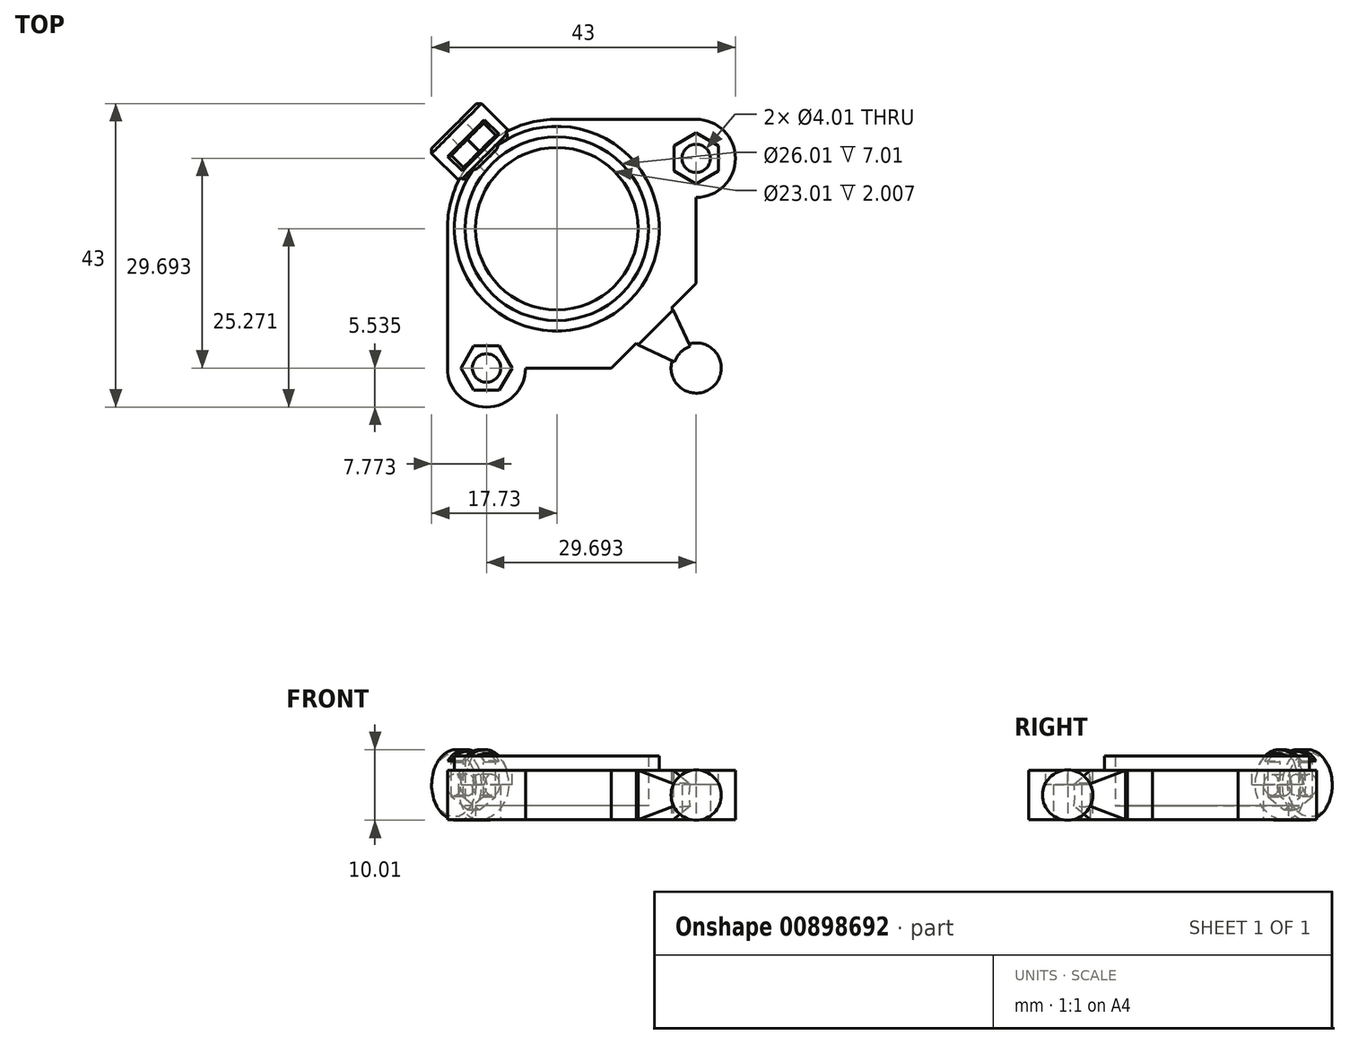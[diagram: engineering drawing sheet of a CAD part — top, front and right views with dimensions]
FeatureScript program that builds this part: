
annotation { "Feature Type Name" : "Feature", "Feature Type Description" : "" }
export const myFeature = defineFeature(function(context is Context, id is Id, definition is map)
    precondition{}
    {
        {
            var Q0;
            Q0=qCreatedBy(makeId("Top.planeOp"),FACE);
            var sketch = newSketch(context, id + "F0", { "sketchPlane" : qUnion([Q0])});
            skArc(sketch, "E0", {"start": v(3.05, -1.27) * mm, "mid": v(0, 3.3) * mm, "end": v(-3.05, -1.27) * mm, "construction": true});
            skArc(sketch, "E1", {"start": v(-32.87, 34.65) * mm, "mid": v(-35.92, 39.22) * mm, "end": v(-38.97, 34.65) * mm, "construction": true});
            skArc(sketch, "E2", {"start": v(38.97, 34.65) * mm, "mid": v(35.92, 39.22) * mm, "end": v(32.87, 34.65) * mm, "construction": true});
            skCircle(sketch, "E3", {"center": v(0, 35.92) * mm, "radius": 14.29 * mm, "construction": true});
            skArc(sketch, "E4.0", {"start": v(-35.92, 46.84) * mm, "mid": v(-46.06, 39.97) * mm, "end": v(-43.45, 28) * mm, "construction": true});
            skArc(sketch, "E5.0", {"start": v(0, 56.56) * mm, "mid": v(-12.05, 52.67) * mm, "end": v(-19.57, 42.48) * mm, "construction": true});
            skArc(sketch, "E6.0", {"start": v(43.45, 28) * mm, "mid": v(46.06, 39.97) * mm, "end": v(35.92, 46.84) * mm, "construction": true});
            skArc(sketch, "E7.0", {"start": v(-6.65, -7) * mm, "mid": v(-5.57, -7.88) * mm, "end": v(-4.38, -8.6) * mm, "construction": true});
            skLineSegment(sketch, "E8", {"start": v(-35.92, 46.84) * mm, "end": v(-28.3, 46.84) * mm, "construction": true});
            skLineSegment(sketch, "E9", {"start": v(30.37, 46.84) * mm, "end": v(35.92, 46.84) * mm, "construction": true});
            skLineSegment(sketch, "E10", {"start": v(43.45, 28) * mm, "end": v(40.52, 25.22) * mm, "construction": true});
            skLineSegment(sketch, "E11", {"start": v(-6.65, -7) * mm, "end": v(-32.87, 17.95) * mm, "construction": true});
            skCircle(sketch, "E12", {"center": v(-35.92, 35.92) * mm, "radius": 3.05 * mm, "construction": true});
            skCircle(sketch, "E13", {"center": v(35.92, 35.92) * mm, "radius": 3.05 * mm, "construction": true});
            skCircle(sketch, "E14", {"center": v(0, 0) * mm, "radius": 3.05 * mm, "construction": true});
            skLineSegment(sketch, "E15", {"start": v(-32.87, 35.92) * mm, "end": v(-32.87, 17.95) * mm, "construction": true});
            skLineSegment(sketch, "E16", {"start": v(-38.97, 35.92) * mm, "end": v(-38.97, 25.88) * mm, "construction": true});
            skLineSegment(sketch, "E17", {"start": v(-3.05, 0) * mm, "end": v(-3.05, -7.79) * mm, "construction": true});
            skLineSegment(sketch, "E18", {"start": v(3.05, 0) * mm, "end": v(3.05, -7.79) * mm, "construction": true});
            skPoint(sketch, "E19", {"position": v(-3.05, -1.27) * mm});
            skPoint(sketch, "E20", {"position": v(3.05, -1.27) * mm});
            skArc(sketch, "E21.trimOffspring", {"start": v(4.38, -8.6) * mm, "mid": v(5.57, -7.88) * mm, "end": v(6.65, -7) * mm, "construction": true});
            skLineSegment(sketch, "E22.trimOffspring", {"start": v(-40.52, 25.22) * mm, "end": v(-43.45, 28) * mm, "construction": true});
            skPoint(sketch, "E23.visualSharp", {"position": v(-38.97, 23.75) * mm});
            skArc(sketch, "E23.filletArc", {"start": v(-40.52, 25.22) * mm, "mid": v(-39.52, 25.04) * mm, "end": v(-38.97, 25.88) * mm, "construction": true});
            skPoint(sketch, "E24.visualSharp", {"position": v(-3.05, -9.16) * mm});
            skArc(sketch, "E24.filletArc", {"start": v(-4.38, -8.6) * mm, "mid": v(-3.49, -8.57) * mm, "end": v(-3.05, -7.79) * mm, "construction": true});
            skPoint(sketch, "E25.visualSharp", {"position": v(3.05, -9.16) * mm});
            skArc(sketch, "E25.filletArc", {"start": v(3.05, -7.79) * mm, "mid": v(3.49, -8.57) * mm, "end": v(4.38, -8.6) * mm, "construction": true});
            skLineSegment(sketch, "E26", {"start": v(32.87, 35.92) * mm, "end": v(32.87, 17.95) * mm, "construction": true});
            skLineSegment(sketch, "E27", {"start": v(38.97, 35.92) * mm, "end": v(38.97, 25.88) * mm, "construction": true});
            skLineSegment(sketch, "E28.trimOffspring", {"start": v(32.87, 17.95) * mm, "end": v(6.65, -7) * mm, "construction": true});
            skPoint(sketch, "E29.visualSharp", {"position": v(38.97, 23.75) * mm});
            skArc(sketch, "E30.filletArc", {"start": v(38.97, 25.88) * mm, "mid": v(39.52, 25.04) * mm, "end": v(40.52, 25.22) * mm, "construction": true});
            skLineSegment(sketch, "E31", {"start": v(-35.92, 35.92) * mm, "end": v(35.92, 35.92) * mm, "construction": true});
            skArc(sketch, "E32.trimOffspring", {"start": v(-19.57, 42.48) * mm, "mid": v(-23.42, 45.7) * mm, "end": v(-28.3, 46.84) * mm, "construction": true});
            skCircle(sketch, "E33", {"center": v(-9.96, 16.19) * mm, "radius": 2 * mm});
            skCircle(sketch, "E34", {"center": v(19.74, 45.88) * mm, "radius": 2 * mm});
            skPoint(sketch, "E35.start.orphan", {"position": v(0, 56.56) * mm});
            skLineSegment(sketch, "E36", {"start": v(0, 56.56) * mm, "end": v(19.74, 56.56) * mm, "construction": true});
            skArc(sketch, "E37.trimOffspring", {"start": v(30.37, 46.84) * mm, "mid": v(26.94, 53.76) * mm, "end": v(19.74, 56.56) * mm, "construction": true});
            skArc(sketch, "E38", {"start": v(0, 51.41) * mm, "mid": v(-10.96, 46.88) * mm, "end": v(-15.5, 35.92) * mm});
            skCircle(sketch, "E39", {"center": v(0, 35.92) * mm, "radius": 11.5 * mm});
            skArc(sketch, "E40", {"start": v(-15.5, 16.19) * mm, "mid": v(-9.96, 10.65) * mm, "end": v(-4.42, 16.19) * mm});
            skArc(sketch, "E41", {"start": v(19.74, 40.34) * mm, "mid": v(25.27, 45.88) * mm, "end": v(19.74, 51.41) * mm});
            skLineSegment(sketch, "E42", {"start": v(-15.5, 35.92) * mm, "end": v(-15.5, 16.19) * mm});
            skLineSegment(sketch, "E43", {"start": v(0, 51.41) * mm, "end": v(19.74, 51.41) * mm});
            skLineSegment(sketch, "E44", {"start": v(-4.42, 16.19) * mm, "end": v(7.74, 16.19) * mm});
            skLineSegment(sketch, "E45", {"start": v(19.74, 28.18) * mm, "end": v(19.74, 40.34) * mm});
            skLineSegment(sketch, "E46", {"start": v(19.74, 28.18) * mm, "end": v(7.74, 16.19) * mm});
            skCircle(sketch, "E47", {"center": v(0, 35.92) * mm, "radius": 13 * mm});
            skPoint(sketch, "E48.orphan", {"position": v(19.74, 16.19) * mm});
            skLineSegment(sketch, "E49", {"start": v(0, 35.92) * mm, "end": v(19.74, 16.19) * mm, "construction": true});
            skLineSegment(sketch, "E50", {"start": v(11.26, 19.7) * mm, "end": v(17.26, 13.7) * mm});
            skLineSegment(sketch, "E51", {"start": v(17.26, 13.7) * mm, "end": v(22.21, 18.66) * mm});
            skLineSegment(sketch, "E52", {"start": v(22.21, 18.66) * mm, "end": v(16.22, 24.66) * mm});
            skSolve(sketch);
        }
        {
            var Q0;
            Q0=makeQuery(id+"F0.imprint","IMPRINT",FACE,{"disambiguationData":[TD([[makeQuery(id+"F0.imprint","IMPRINT",EDGE,{"derivedFrom":sQuery(id+"F0.wireOp",EDGE,"E33")}),-1.0]])]});
            var Q1;
            {var subQ0=sQuery(id+"F0.wireOp",EDGE,"E50");Q1=makeQuery(id+"F0.imprint","IMPRINT",FACE,{"disambiguationData":[TD([[makeQuery(id+"F0.imprint","IMPRINT",EDGE,{"derivedFrom":subQ0}),1.0]])]});}
            extrude(context, id + "F1", {"entities" : qUnion([Q0, Q1]), "depth" : 7 * mm, "offsetDistance" : 25.4 * mm});
        }
        {
            var Q0;
            Q0=makeQuery(id+"F1.opExtrude","CAP_EDGE",EDGE,{"disambiguationData":[OSD([sQuery(id+"F0.wireOp",EDGE,"E51")])],"isStart":false});
            var Q1;
            Q1=makeQuery(id+"F1.opExtrude","SWEPT_EDGE",EDGE,{"disambiguationData":[OSD([sQuery(id+"F0.wireOp",EDGE,"E51"),sQuery(id+"F0.wireOp",EDGE,"E52")])]});
            var Q2;
            Q2=makeQuery(id+"F1.opExtrude","SWEPT_EDGE",EDGE,{"disambiguationData":[OSD([sQuery(id+"F0.wireOp",EDGE,"E50"),sQuery(id+"F0.wireOp",EDGE,"E51")])]});
            var Q3;
            Q3=makeQuery(id+"F1.opExtrude","CAP_EDGE",EDGE,{"disambiguationData":[OSD([sQuery(id+"F0.wireOp",EDGE,"E51")])],"isStart":true});
            chamfer(context, id + "F2", {"entities" : qUnion([Q0, Q1, Q2, Q3]), "chamferType" : ChamferType.OFFSET_ANGLE, "width" : 8.13 * mm, "oppositeDirection" : false, "angle" : 20 * degree, "tangentPropagation" : true});
        }
        {
            var Q0;
            Q0=makeQuery(id+"F0.imprint","IMPRINT",FACE,{"disambiguationData":[TD([[makeQuery(id+"F0.imprint","IMPRINT",EDGE,{"derivedFrom":sQuery(id+"F0.wireOp",EDGE,"E39")}),-1.0]])]});
            extrude(context, id + "F3", {"entities" : qUnion([Q0]), "operationType" : NewBodyOperationType.ADD, "depth" : 2 * mm, "offsetDistance" : 25.4 * mm});
        }
        {
            var Q0;
            Q0=makeQuery(id+"F1.opExtrude","CAP_FACE",FACE,{"disambiguationData":[OSD([sQuery(id+"F0.wireOp",EDGE,"E33"),sQuery(id+"F0.wireOp",EDGE,"E34"),sQuery(id+"F0.wireOp",EDGE,"E38"),sQuery(id+"F0.wireOp",EDGE,"E40"),sQuery(id+"F0.wireOp",EDGE,"E41"),sQuery(id+"F0.wireOp",EDGE,"E42"),sQuery(id+"F0.wireOp",EDGE,"E43"),sQuery(id+"F0.wireOp",EDGE,"E44"),sQuery(id+"F0.wireOp",EDGE,"E45"),sQuery(id+"F0.wireOp",EDGE,"E46"),sQuery(id+"F0.wireOp",EDGE,"E47"),sQuery(id+"F0.wireOp",EDGE,"E50"),sQuery(id+"F0.wireOp",EDGE,"E51"),sQuery(id+"F0.wireOp",EDGE,"E52")])],"isStart":false});
            var sketch = newSketch(context, id + "F4", { "sketchPlane" : qUnion([Q0])});
            skCircle(sketch, "E53", {"center": v(0, 35.92) * mm, "radius": 14.5 * mm});
            skCircle(sketch, "E54.cCircle", {"center": v(19.74, 45.88) * mm, "radius": 3.6 * mm, "construction": true});
            skLineSegment(sketch, "E54.0", {"start": v(19.74, 42.27) * mm, "end": v(16.61, 44.07) * mm});
            skLineSegment(sketch, "E54.1", {"start": v(16.61, 44.07) * mm, "end": v(16.61, 47.68) * mm});
            skLineSegment(sketch, "E54.2", {"start": v(16.61, 47.68) * mm, "end": v(19.74, 49.48) * mm});
            skLineSegment(sketch, "E54.3", {"start": v(19.74, 49.48) * mm, "end": v(22.86, 47.68) * mm});
            skLineSegment(sketch, "E54.4", {"start": v(22.86, 47.68) * mm, "end": v(22.86, 44.07) * mm});
            skLineSegment(sketch, "E54.5", {"start": v(22.86, 44.07) * mm, "end": v(19.74, 42.27) * mm});
            skCircle(sketch, "E55.cCircle", {"center": v(-9.96, 16.19) * mm, "radius": 3.6 * mm, "construction": true});
            skLineSegment(sketch, "E55.0", {"start": v(-6.35, 16.19) * mm, "end": v(-8.15, 13.06) * mm});
            skLineSegment(sketch, "E55.1", {"start": v(-8.15, 13.06) * mm, "end": v(-11.76, 13.06) * mm});
            skLineSegment(sketch, "E55.2", {"start": v(-11.76, 13.06) * mm, "end": v(-13.56, 16.19) * mm});
            skLineSegment(sketch, "E55.3", {"start": v(-13.56, 16.19) * mm, "end": v(-11.76, 19.3) * mm});
            skLineSegment(sketch, "E55.4", {"start": v(-11.76, 19.3) * mm, "end": v(-8.15, 19.3) * mm});
            skLineSegment(sketch, "E55.5", {"start": v(-8.15, 19.3) * mm, "end": v(-6.35, 16.19) * mm});
            skSolve(sketch);
        }
        {
            var Q0;
            Q0=makeQuery(id+"F4.imprint","IMPRINT",FACE,{"disambiguationData":[TD([[makeQuery(id+"F4.imprint","IMPRINT",EDGE,{"derivedFrom":sQuery(id+"F4.wireOp",EDGE,"E53")}),1.0]])]});
            extrude(context, id + "F5", {"entities" : qUnion([Q0]), "operationType" : NewBodyOperationType.ADD, "depth" : 2 * mm, "offsetDistance" : 25.4 * mm});
        }
        {
            var Q0;
            Q0=makeQuery(id+"F4.imprint","IMPRINT",FACE,{"disambiguationData":[TD([[makeQuery(id+"F4.imprint","IMPRINT",EDGE,{"derivedFrom":sQuery(id+"F4.wireOp",EDGE,"E54.0")}),-1.0]])]});
            var Q1;
            Q1=makeQuery(id+"F4.imprint","IMPRINT",FACE,{"disambiguationData":[TD([[makeQuery(id+"F4.imprint","IMPRINT",EDGE,{"derivedFrom":sQuery(id+"F4.wireOp",EDGE,"E55.0")}),-1.0]])]});
            extrude(context, id + "F6", {"entities" : qUnion([Q0, Q1]), "operationType" : NewBodyOperationType.REMOVE, "oppositeDirection" : true, "depth" : 2 * mm, "offsetDistance" : 25.4 * mm});
        }
        {
            var Q0;
            Q0=makeQuery(id+"F1.opExtrude","SWEPT_FACE",FACE,{"disambiguationData":[OSD([sQuery(id+"F0.wireOp",EDGE,"E51")])]});
            var sketch = newSketch(context, id + "F7", { "sketchPlane" : qUnion([Q0])});
            skArc(sketch, "E56", {"start": v(25.4, 7.06) * mm, "mid": v(21.84, 3.5) * mm, "end": v(25.4, -0.05) * mm});
            skPoint(sketch, "E56.centerSnap0", {"position": v(25.95, 3.5) * mm});
            skPoint(sketch, "E56.centerSnap1", {"position": v(25.4, 4.05) * mm});
            skLineSegment(sketch, "E57", {"start": v(25.4, 7.06) * mm, "end": v(25.4, -0.05) * mm});
            skPoint(sketch, "E57.startSnap0", {"position": v(25.4, 2.96) * mm});
            skSolve(sketch);
        }
        {
            var Q0;
            {var subQ4=sQuery(id+"F7.wireOp",EDGE,"E56");Q0=makeQuery(id+"F7.imprint","IMPRINT",FACE,{"disambiguationData":[TD([[makeQuery(id+"F7.imprint","IMPRINT",EDGE,{"derivedFrom":subQ4}),1.0]])]});}
            var Q1;
            {var subQ1=sQuery(id+"F0.wireOp",EDGE,"E51");var subQ2=makeQuery(id+"F1.opExtrude","SWEPT_FACE",FACE,{"disambiguationData":[OSD([subQ1])]});var subQ7=makeQuery(id+"F2.opChamfer","BLEND_EDGE",EDGE,{"blendedFrom":[makeQuery(id+"F1.opExtrude","SWEPT_EDGE",EDGE,{"disambiguationData":[OSD([sQuery(id+"F0.wireOp",EDGE,"E50"),subQ1])]}),subQ2],"blendedInto":[subQ2]});Q1=makeQuery(id+"F7.imprint","IMPRINT",FACE,{"disambiguationData":[TD([[makeQuery(id+"F7.imprint","IMPRINT",EDGE,{"derivedFrom":subQ7}),1.0]])]});}
            var Q2;
            Q2=sQuery(id+"F7.wireOp",EDGE,"E57");
            revolve(context, id + "F8", {"operationType" : NewBodyOperationType.ADD, "surfaceOperationType" : NewSurfaceOperationType.NEW, "entities" : qUnion([Q0, Q1]), "axis" : qUnion([Q2]), "revolveType" : RevolveType.FULL});
        }
        {
            var Q0;
            {var subQ0=sQuery(id+"F0.wireOp",EDGE,"E46");Q0=makeQuery(id+"F1.opExtrude","SWEPT_FACE",FACE,{"disambiguationData":[OSD([subQ0]),TDD([makeQuery(id+"F0.imprint","IMPRINT",EDGE,{"disambiguationData":[TD([[makeQuery(id+"F0.imprint","INTERSECT",VERTEX,{"derivedFrom":[sQuery(id+"F0.wireOp",EDGE,"E45"),subQ0]}),-1.0]])],"derivedFrom":subQ0})])]});}
            cPlane(context, id + "F9", {"entities" : qUnion([Q0]), "cplaneType" : CPlaneType.OFFSET, "offset" : 40 * mm, "oppositeDirection" : true, "width" : 152.4 * mm, "height" : 152.4 * mm});
        }
        {
            var Q0;
            Q0=qCreatedBy(id+"F9.planeOp",FACE);
            var sketch = newSketch(context, id + "F10", { "sketchPlane" : qUnion([Q0])});
            skCircle(sketch, "E58", {"center": v(25.4, 3.5) * mm, "radius": 3.56 * mm, "construction": true});
            skCircle(sketch, "E59", {"center": v(25.4, 4.95) * mm, "radius": 1.5 * mm});
            skCircle(sketch, "E60", {"center": v(25.4, 4.95) * mm, "radius": 5 * mm});
            skLineSegment(sketch, "E61", {"start": v(31, 0) * mm, "end": v(18.63, -0.11) * mm, "construction": true});
            skLineSegment(sketch, "E62", {"start": v(25.4, 4.95) * mm, "end": v(25.4, 3.5) * mm, "construction": true});
            skSolve(sketch);
        }
        {
            var Q0;
            Q0=makeQuery(id+"F10.imprint","IMPRINT",FACE,{"disambiguationData":[TD([[makeQuery(id+"F10.imprint","IMPRINT",EDGE,{"derivedFrom":sQuery(id+"F10.wireOp",EDGE,"E59")}),-1.0]])]});
            extrude(context, id + "F11", {"entities" : qUnion([Q0]), "operationType" : NewBodyOperationType.ADD, "depth" : 6.6 * mm, "offsetDistance" : 25.4 * mm});
        }
        {
            var Q0;
            Q0=makeQuery(id+"F10.imprint","IMPRINT",FACE,{"disambiguationData":[TD([[makeQuery(id+"F10.imprint","IMPRINT",EDGE,{"derivedFrom":sQuery(id+"F10.wireOp",EDGE,"E59")}),1.0]])]});
            extrude(context, id + "F12", {"entities" : qUnion([Q0]), "operationType" : NewBodyOperationType.REMOVE, "depth" : 12.7 * mm, "offsetDistance" : 25.4 * mm});
        }
        {
            var Q0;
            {var subQ0=sQuery(id+"F10.wireOp",EDGE,"E60");Q0=makeQuery(id+"F11.boolean.opBoolean","SPLIT",EDGE,{"disambiguationData":[TD([makeQuery(id+"F5.opExtrude","CAP_FACE",FACE,{"disambiguationData":[OSD([sQuery(id+"F0.wireOp",EDGE,"E47"),sQuery(id+"F4.wireOp",EDGE,"E53")])],"isStart":false})])],"derivedFrom":makeQuery(id+"F11.opExtrude","CAP_EDGE",EDGE,{"disambiguationData":[OSD([subQ0])],"isStart":false})});}
            var Q1;
            Q1=makeQuery(id+"F11.opExtrude","CAP_EDGE",EDGE,{"disambiguationData":[OSD([sQuery(id+"F10.wireOp",EDGE,"E60")])],"isStart":true});
            chamfer(context, id + "F13", {"entities" : qUnion([Q0, Q1]), "width" : 0.5 * mm, "tangentPropagation" : true});
        }
        {
            var Q0;
            Q0=qCreatedBy(makeId("Top.planeOp"),FACE);
            cPlane(context, id + "F14", {"entities" : qUnion([Q0]), "cplaneType" : CPlaneType.OFFSET, "offset" : 10 * mm, "width" : 152.4 * mm, "height" : 152.4 * mm});
        }
        {
            var Q0;
            Q0=qCreatedBy(id+"F14.planeOp",FACE);
            var sketch = newSketch(context, id + "F15", { "sketchPlane" : qUnion([Q0])});
            skArc(sketch, "E63.0", {"start": v(0, 51.41) * mm, "mid": v(-10.96, 46.88) * mm, "end": v(-15.5, 35.92) * mm, "construction": true});
            skLineSegment(sketch, "E64", {"start": v(-13.25, 44.59) * mm, "end": v(-8.67, 49.17) * mm});
            skLineSegment(sketch, "E65", {"start": v(-13.25, 44.59) * mm, "end": v(-14.95, 46.3) * mm});
            skLineSegment(sketch, "E66", {"start": v(-14.95, 46.3) * mm, "end": v(-10.37, 50.87) * mm});
            skLineSegment(sketch, "E67", {"start": v(-10.37, 50.87) * mm, "end": v(-8.67, 49.17) * mm});
            skLineSegment(sketch, "E68", {"start": v(0, 35.92) * mm, "end": v(-10.96, 46.88) * mm, "construction": true});
            skLineSegment(sketch, "E69", {"start": v(-10.37, 50.87) * mm, "end": v(0, 51.41) * mm, "construction": true});
            skLineSegment(sketch, "E70", {"start": v(-14.95, 46.3) * mm, "end": v(-15.5, 35.92) * mm, "construction": true});
            skSolve(sketch);
        }
        {
            var Q0;
            Q0=makeQuery(id+"F15.imprint","IMPRINT",FACE,{"disambiguationData":[TD([[makeQuery(id+"F15.imprint","IMPRINT",EDGE,{"derivedFrom":sQuery(id+"F15.wireOp",EDGE,"E64")}),1.0]])]});
            extrude(context, id + "F16", {"entities" : qUnion([Q0]), "operationType" : NewBodyOperationType.REMOVE, "oppositeDirection" : true, "depth" : 8.6 * mm, "offsetDistance" : 25.4 * mm});
        }
        {
            var Q0;
            Q0=makeQuery(id+"F16.boolean.opBoolean","COPY",EDGE,{"derivedFrom":makeQuery(id+"F16.opExtrude","CAP_EDGE",EDGE,{"disambiguationData":[OSD([sQuery(id+"F15.wireOp",EDGE,"E67")])],"isStart":false})});
            var Q1;
            Q1=makeQuery(id+"F16.boolean.opBoolean","COPY",EDGE,{"derivedFrom":makeQuery(id+"F16.opExtrude","CAP_EDGE",EDGE,{"disambiguationData":[OSD([sQuery(id+"F15.wireOp",EDGE,"E65")])],"isStart":false})});
            chamfer(context, id + "F17", {"entities" : qUnion([Q0, Q1]), "chamferType" : ChamferType.OFFSET_ANGLE, "width" : 1.85 * mm, "oppositeDirection" : false, "angle" : 60 * degree, "tangentPropagation" : true});
        }
        {
            var Q0;
            Q0=makeQuery(id+"F16.boolean.opBoolean","INTERSECT",EDGE,{"derivedFrom":[makeQuery(id+"F11.opExtrude","SWEPT_FACE",FACE,{"disambiguationData":[OSD([sQuery(id+"F10.wireOp",EDGE,"E60")])]}),makeQuery(id+"F16.opExtrude","SWEPT_FACE",FACE,{"disambiguationData":[OSD([sQuery(id+"F15.wireOp",EDGE,"E66")])]})]});
            var Q1;
            Q1=makeQuery(id+"F16.boolean.opBoolean","INTERSECT",EDGE,{"derivedFrom":[makeQuery(id+"F11.opExtrude","SWEPT_FACE",FACE,{"disambiguationData":[OSD([sQuery(id+"F10.wireOp",EDGE,"E60")])]}),makeQuery(id+"F16.opExtrude","SWEPT_FACE",FACE,{"disambiguationData":[OSD([sQuery(id+"F15.wireOp",EDGE,"E65")])]})]});
            var Q2;
            Q2=makeQuery(id+"F16.boolean.opBoolean","INTERSECT",EDGE,{"derivedFrom":[makeQuery(id+"F11.opExtrude","SWEPT_FACE",FACE,{"disambiguationData":[OSD([sQuery(id+"F10.wireOp",EDGE,"E60")])]}),makeQuery(id+"F16.opExtrude","SWEPT_FACE",FACE,{"disambiguationData":[OSD([sQuery(id+"F15.wireOp",EDGE,"E64")])]})]});
            var Q3;
            Q3=makeQuery(id+"F16.boolean.opBoolean","INTERSECT",EDGE,{"derivedFrom":[makeQuery(id+"F11.opExtrude","SWEPT_FACE",FACE,{"disambiguationData":[OSD([sQuery(id+"F10.wireOp",EDGE,"E60")])]}),makeQuery(id+"F16.opExtrude","SWEPT_FACE",FACE,{"disambiguationData":[OSD([sQuery(id+"F15.wireOp",EDGE,"E67")])]})]});
            chamfer(context, id + "F18", {"entities" : qUnion([Q0, Q1, Q2, Q3]), "width" : 0.25 * mm, "tangentPropagation" : true});
        }
    });
